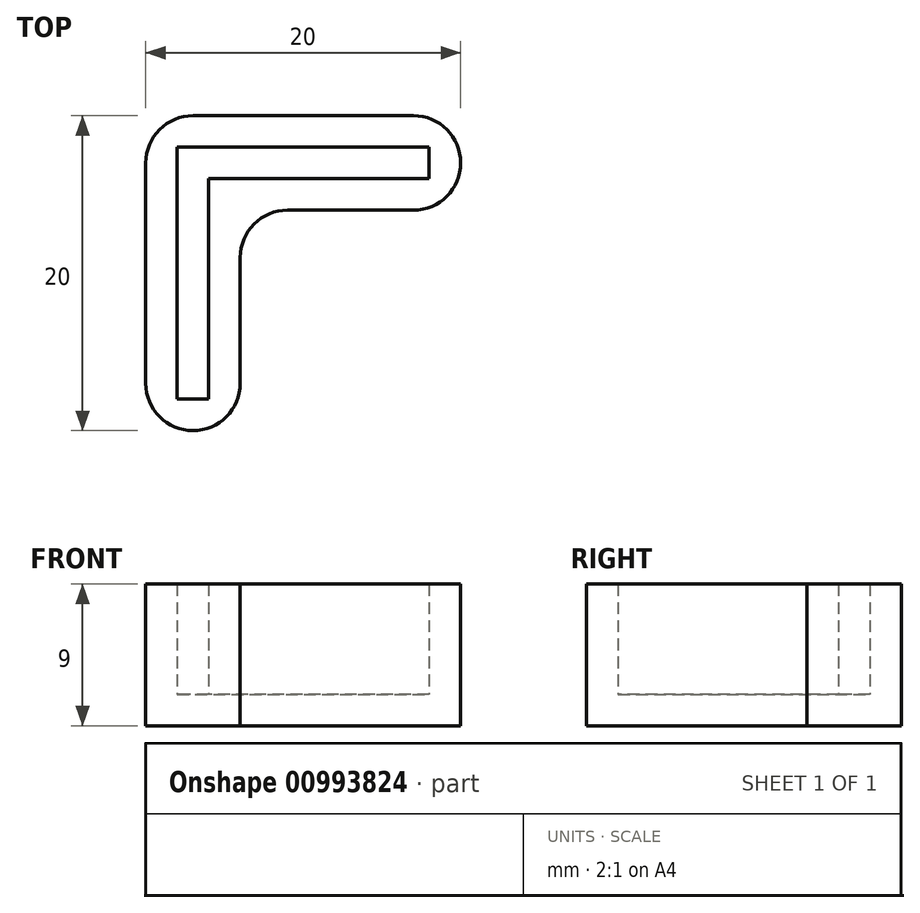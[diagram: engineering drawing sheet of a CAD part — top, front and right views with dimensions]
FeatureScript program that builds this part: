
annotation { "Feature Type Name" : "Feature", "Feature Type Description" : "" }
export const myFeature = defineFeature(function(context is Context, id is Id, definition is map)
    precondition{}
    {
        {
            var Q0;
            Q0=qCreatedBy(makeId("Top.planeOp"),FACE);
            var sketch = newSketch(context, id + "F0", { "sketchPlane" : qUnion([Q0])});
            skLineSegment(sketch, "E0", {"start": v(-7.72, 7) * mm, "end": v(10.28, 7) * mm});
            skLineSegment(sketch, "E1", {"start": v(10.28, 7) * mm, "end": v(10.28, 1) * mm});
            skLineSegment(sketch, "E2", {"start": v(10.28, 1) * mm, "end": v(-1.72, 1) * mm});
            skLineSegment(sketch, "E3", {"start": v(-1.72, 1) * mm, "end": v(-1.72, -11) * mm});
            skLineSegment(sketch, "E4", {"start": v(-1.72, -11) * mm, "end": v(-7.72, -11) * mm});
            skLineSegment(sketch, "E5", {"start": v(-7.72, -11) * mm, "end": v(-7.72, 7) * mm});
            skLineSegment(sketch, "E6", {"start": v(-5.72, -11) * mm, "end": v(-5.72, 5) * mm});
            skLineSegment(sketch, "E7", {"start": v(-5.72, 5) * mm, "end": v(10.28, 5) * mm});
            skLineSegment(sketch, "E8", {"start": v(10.28, 3) * mm, "end": v(-3.72, 3) * mm});
            skLineSegment(sketch, "E9", {"start": v(-3.72, 3) * mm, "end": v(-3.72, -11) * mm});
            skLineSegment(sketch, "E10", {"start": v(-3.72, -11) * mm, "end": v(-1.72, -11) * mm});
            skLineSegment(sketch, "E11", {"start": v(-5.72, -11) * mm, "end": v(-7.72, -11) * mm});
            skLineSegment(sketch, "E12", {"start": v(10.28, 1) * mm, "end": v(10.28, 3) * mm});
            skLineSegment(sketch, "E13", {"start": v(10.28, 5) * mm, "end": v(10.28, 7) * mm});
            skLineSegment(sketch, "E14.bottom", {"start": v(-7.72, -11) * mm, "end": v(-1.72, -11) * mm});
            skLineSegment(sketch, "E14.top", {"start": v(-7.72, -13) * mm, "end": v(-1.72, -13) * mm});
            skLineSegment(sketch, "E14.left", {"start": v(-7.72, -11) * mm, "end": v(-7.72, -13) * mm});
            skLineSegment(sketch, "E14.right", {"start": v(-1.72, -11) * mm, "end": v(-1.72, -13) * mm});
            skLineSegment(sketch, "E15.bottom", {"start": v(10.28, 7) * mm, "end": v(12.28, 7) * mm});
            skLineSegment(sketch, "E15.top", {"start": v(10.28, 1) * mm, "end": v(12.28, 1) * mm});
            skLineSegment(sketch, "E15.right", {"start": v(12.28, 7) * mm, "end": v(12.28, 1) * mm});
            skSolve(sketch);
        }
        {
            var Q0;
            Q0=makeQuery(id+"F0.imprint","IMPRINT",FACE,{"disambiguationData":[TD([[makeQuery(id+"F0.imprint","IMPRINT",EDGE,{"derivedFrom":sQuery(id+"F0.wireOp",EDGE,"E0")}),-1.0]])]});
            var Q1;
            Q1=makeQuery(id+"F0.imprint","IMPRINT",FACE,{"disambiguationData":[TD([[makeQuery(id+"F0.imprint","IMPRINT",EDGE,{"derivedFrom":sQuery(id+"F0.wireOp",EDGE,"E1")}),-1.0]])]});
            var Q2;
            Q2=makeQuery(id+"F0.imprint","IMPRINT",FACE,{"disambiguationData":[TD([[makeQuery(id+"F0.imprint","IMPRINT",EDGE,{"derivedFrom":sQuery(id+"F0.wireOp",EDGE,"E2")}),-1.0]])]});
            var Q3;
            {var subQ3=sQuery(id+"F0.wireOp",EDGE,"E15.bottom");Q3=makeQuery(id+"F0.imprint","IMPRINT",FACE,{"disambiguationData":[TD([[makeQuery(id+"F0.imprint","IMPRINT",EDGE,{"derivedFrom":subQ3}),-1.0]])]});}
            var Q4;
            Q4=makeQuery(id+"F0.imprint","IMPRINT",FACE,{"disambiguationData":[TD([[makeQuery(id+"F0.imprint","IMPRINT",EDGE,{"derivedFrom":sQuery(id+"F0.wireOp",EDGE,"E14.top")}),1.0]])]});
            var Q5;
            {var subQ4=sQuery(id+"F0.wireOp",EDGE,"E6");Q5=makeQuery(id+"F0.imprint","IMPRINT",FACE,{"disambiguationData":[TD([[makeQuery(id+"F0.imprint","IMPRINT",EDGE,{"derivedFrom":subQ4}),-1.0]])]});}
            extrude(context, id + "F1", {"entities" : qUnion([Q0, Q1, Q2, Q3, Q4, Q5]), "oppositeDirection" : true, "depth" : 2 * mm, "offsetDistance" : 25 * mm});
        }
        {
            var Q0;
            Q0=makeQuery(id+"F0.imprint","IMPRINT",FACE,{"disambiguationData":[TD([[makeQuery(id+"F0.imprint","IMPRINT",EDGE,{"derivedFrom":sQuery(id+"F0.wireOp",EDGE,"E0")}),-1.0]])]});
            var Q1;
            Q1=makeQuery(id+"F0.imprint","IMPRINT",FACE,{"disambiguationData":[TD([[makeQuery(id+"F0.imprint","IMPRINT",EDGE,{"derivedFrom":sQuery(id+"F0.wireOp",EDGE,"E2")}),-1.0]])]});
            var Q2;
            {var subQ3=sQuery(id+"F0.wireOp",EDGE,"E15.bottom");Q2=makeQuery(id+"F0.imprint","IMPRINT",FACE,{"disambiguationData":[TD([[makeQuery(id+"F0.imprint","IMPRINT",EDGE,{"derivedFrom":subQ3}),-1.0]])]});}
            var Q3;
            Q3=makeQuery(id+"F0.imprint","IMPRINT",FACE,{"disambiguationData":[TD([[makeQuery(id+"F0.imprint","IMPRINT",EDGE,{"derivedFrom":sQuery(id+"F0.wireOp",EDGE,"E14.top")}),1.0]])]});
            extrude(context, id + "F2", {"entities" : qUnion([Q0, Q1, Q2, Q3]), "operationType" : NewBodyOperationType.ADD, "depth" : 7 * mm, "offsetDistance" : 25 * mm});
        }
        {
            var Q0;
            {var subQ0=sQuery(id+"F0.wireOp",EDGE,"E3");var subQ1=sQuery(id+"F0.wireOp",EDGE,"E2");Q0=makeQuery(id+"F2.boolean.opBoolean","MERGE",EDGE,{"derivedFrom":[makeQuery(id+"F1.opExtrude","SWEPT_EDGE",EDGE,{"disambiguationData":[OSD([subQ1,subQ0])]}),makeQuery(id+"F2.opExtrude","SWEPT_EDGE",EDGE,{"disambiguationData":[OSD([subQ1,subQ0])]})]});}
            var Q1;
            {var subQ0=sQuery(id+"F0.wireOp",EDGE,"E5");var subQ1=sQuery(id+"F0.wireOp",EDGE,"E0");Q1=makeQuery(id+"F2.boolean.opBoolean","MERGE",EDGE,{"derivedFrom":[makeQuery(id+"F1.opExtrude","SWEPT_EDGE",EDGE,{"disambiguationData":[OSD([subQ1,subQ0])]}),makeQuery(id+"F2.opExtrude","SWEPT_EDGE",EDGE,{"disambiguationData":[OSD([subQ1,subQ0])]})]});}
            var Q2;
            {var subQ0=sQuery(id+"F0.wireOp",EDGE,"E14.left");var subQ1=sQuery(id+"F0.wireOp",EDGE,"E14.top");Q2=makeQuery(id+"F2.boolean.opBoolean","MERGE",EDGE,{"derivedFrom":[makeQuery(id+"F1.opExtrude","SWEPT_EDGE",EDGE,{"disambiguationData":[OSD([subQ1,subQ0])]}),makeQuery(id+"F2.opExtrude","SWEPT_EDGE",EDGE,{"disambiguationData":[OSD([subQ1,subQ0])]})]});}
            var Q3;
            {var subQ0=sQuery(id+"F0.wireOp",EDGE,"E14.right");var subQ1=sQuery(id+"F0.wireOp",EDGE,"E14.top");Q3=makeQuery(id+"F2.boolean.opBoolean","MERGE",EDGE,{"derivedFrom":[makeQuery(id+"F1.opExtrude","SWEPT_EDGE",EDGE,{"disambiguationData":[OSD([subQ1,subQ0])]}),makeQuery(id+"F2.opExtrude","SWEPT_EDGE",EDGE,{"disambiguationData":[OSD([subQ1,subQ0])]})]});}
            var Q4;
            {var subQ0=sQuery(id+"F0.wireOp",EDGE,"E15.right");var subQ1=sQuery(id+"F0.wireOp",EDGE,"E15.top");Q4=makeQuery(id+"F2.boolean.opBoolean","MERGE",EDGE,{"derivedFrom":[makeQuery(id+"F1.opExtrude","SWEPT_EDGE",EDGE,{"disambiguationData":[OSD([subQ1,subQ0])]}),makeQuery(id+"F2.opExtrude","SWEPT_EDGE",EDGE,{"disambiguationData":[OSD([subQ1,subQ0])]})]});}
            var Q5;
            {var subQ0=sQuery(id+"F0.wireOp",EDGE,"E15.right");var subQ1=sQuery(id+"F0.wireOp",EDGE,"E15.bottom");Q5=makeQuery(id+"F2.boolean.opBoolean","MERGE",EDGE,{"derivedFrom":[makeQuery(id+"F1.opExtrude","SWEPT_EDGE",EDGE,{"disambiguationData":[OSD([subQ1,subQ0])]}),makeQuery(id+"F2.opExtrude","SWEPT_EDGE",EDGE,{"disambiguationData":[OSD([subQ1,subQ0])]})]});}
            fillet(context, id + "F3", {"entities" : qUnion([Q0, Q1, Q2, Q3, Q4, Q5]), "radius" : 3 * mm, "tangentPropagation" : true, "allowEdgeOverflow" : false});
        }
    });
